# Revit family: Furniture_Table_Spacestor_Arc Boardroom Table
name_source: partatom
category: Furniture
revit_build: Autodesk Revit 2015 (Build: 20140223_1515(x64)
units: mm (PartAtom-declared; Revit-internal decimal feet)

## types (23) — shared parameters
Polished Steel = Spacestor Polished Steel
Table Top = Spacestor White

## per-type parameters (varying)
| type | A | Boat | Bowed Triangle 1200 | Bowed Triangle 800 | Double D End | Leg Length | Leg Width | Length | Offset | Oval | P Length | Rectangular | Single Leg | Split Leg | Split Leg Length | Width |
| rectangular - 1800w x 800d x 720h | 750 mm  [stored 2.46063 ft] | No | No | No | No | 1700 mm  [stored 5.57743 ft] | 700 mm  [stored 2.29659 ft] | 1800 mm  [stored 5.90551 ft] | 520 mm | No | 770 mm  [stored 2.52625 ft] | Yes | Yes | No | 1700 mm  [stored 5.57743 ft] | 800 mm  [stored 2.62467 ft] |
| rectangular - 2000w x 1000d x 720h | 750 mm  [stored 2.46063 ft] | No | No | No | No | 1900 mm  [stored 6.2336 ft] | 900 mm  [stored 2.95276 ft] | 2000 mm  [stored 6.56168 ft] | 520 mm | No | 770 mm  [stored 2.52625 ft] | Yes | Yes | No | 1900 mm  [stored 6.2336 ft] | 1000 mm  [stored 3.28084 ft] |
| rectangular - 2400w x 1200d x 720h | 750 mm  [stored 2.46063 ft] | No | No | No | No | 2300 mm | 1100 mm | 2400 mm | 50 mm  [stored 0.164042 ft] | No | 770 mm  [stored 2.52625 ft] | Yes | Yes | No | 2300 mm | 1200 mm |
| rectangular - 3000w x 1200d x 720h | 800 mm  [stored 2.62467 ft] | No | No | No | No | 2900 mm  [stored 9.51444 ft] | 1100 mm | 3000 mm  [stored 9.84252 ft] | 20 mm  [stored 0.0656168 ft] | No | 770 mm  [stored 2.52625 ft] | Yes | No | Yes | 1400 mm  [stored 4.59318 ft] | 1200 mm |
| rectangular - 3600w x 1200d x 720h | 1100 mm | No | No | No | No | 3500 mm  [stored 11.4829 ft] | 1100 mm | 3600 mm  [stored 11.811 ft] | 20 mm  [stored 0.0656168 ft] | No | 770 mm  [stored 2.52625 ft] | Yes | No | Yes | 1700 mm  [stored 5.57743 ft] | 1200 mm |
| rectangular - 4800w x 1200d x 720h | 1200 mm | No | No | No | No | 4700 mm | 1100 mm | 4800 mm | 520 mm | No | 770 mm  [stored 2.52625 ft] | Yes | No | Yes | 2300 mm | 1200 mm |
| oval-shaped - 2000w x 1000d x 720h | 750 mm  [stored 2.46063 ft] | No | No | No | No | 1300 mm  [stored 4.26509 ft] | 600 mm  [stored 1.9685 ft] | 2000 mm  [stored 6.56168 ft] | 520 mm | Yes | 770 mm  [stored 2.52625 ft] | No | Yes | No | 1900 mm  [stored 6.2336 ft] | 1000 mm  [stored 3.28084 ft] |
| oval-shaped - 2400w x 1200d x 720h | 750 mm  [stored 2.46063 ft] | No | No | No | No | 1700 mm  [stored 5.57743 ft] | 800 mm  [stored 2.62467 ft] | 2400 mm | 520 mm | Yes | 770 mm  [stored 2.52625 ft] | No | Yes | No | 2300 mm | 1200 mm |
| oval-shaped - 3000w x 1200d x 720h | 750 mm  [stored 2.46063 ft] | No | No | No | No | 2300 mm | 800 mm  [stored 2.62467 ft] | 3000 mm  [stored 9.84252 ft] | 520 mm | Yes | 770 mm  [stored 2.52625 ft] | No | Yes | No | 2900 mm  [stored 9.51444 ft] | 1200 mm |
| oval-shaped - 3600w x 1200d x 720h | 750 mm  [stored 2.46063 ft] | No | No | No | No | 2900 mm  [stored 9.51444 ft] | 800 mm  [stored 2.62467 ft] | 3600 mm  [stored 11.811 ft] | 20 mm  [stored 0.0656168 ft] | Yes | 770 mm  [stored 2.52625 ft] | No | No | Yes | 1100 mm | 1200 mm |
| oval-shaped - 4800w x 1200d x 720h | 750 mm  [stored 2.46063 ft] | No | No | No | No | 4100 mm  [stored 13.4514 ft] | 800 mm  [stored 2.62467 ft] | 4800 mm | 520 mm | Yes | 770 mm  [stored 2.52625 ft] | No | No | Yes | 1700 mm  [stored 5.57743 ft] | 1200 mm |
| double d-ended - 2000w x 1200d x 720h | 750 mm  [stored 2.46063 ft] | No | No | No | Yes | 1400 mm  [stored 4.59318 ft] | 1000 mm  [stored 3.28084 ft] | 2000 mm  [stored 6.56168 ft] | 520 mm | No | 770 mm  [stored 2.52625 ft] | No | Yes | No | 1900 mm  [stored 6.2336 ft] | 1200 mm |
| double d-ended - 2400w x 1200d x 720h | 750 mm  [stored 2.46063 ft] | No | No | No | Yes | 1800 mm  [stored 5.90551 ft] | 1000 mm  [stored 3.28084 ft] | 2400 mm | 520 mm | No | 770 mm  [stored 2.52625 ft] | No | Yes | No | 2300 mm | 1200 mm |
| double d-ended - 3000w x 1200d x 720h | 750 mm  [stored 2.46063 ft] | No | No | No | Yes | 2400 mm | 1000 mm  [stored 3.28084 ft] | 3000 mm  [stored 9.84252 ft] | 520 mm | No | 770 mm  [stored 2.52625 ft] | No | Yes | No | 2900 mm  [stored 9.51444 ft] | 1200 mm |
| double d-ended - 3600w x 1200d x 720h | 900 mm  [stored 2.95276 ft] | No | No | No | Yes | 3000 mm  [stored 9.84252 ft] | 1000 mm  [stored 3.28084 ft] | 3600 mm  [stored 11.811 ft] | 20 mm  [stored 0.0656168 ft] | No | 770 mm  [stored 2.52625 ft] | No | No | Yes | 1450 mm  [stored 4.75722 ft] | 1200 mm |
| double d-ended - 4800w x 1200d x 720h | 750 mm  [stored 2.46063 ft] | No | No | No | Yes | 4200 mm | 1000 mm  [stored 3.28084 ft] | 4800 mm | 520 mm | No | 770 mm  [stored 2.52625 ft] | No | No | Yes | 2050 mm  [stored 6.72572 ft] | 1200 mm |
| boat-shaped - 2000w x 1000_800d x 720h | 750 mm  [stored 2.46063 ft] | Yes | No | No | No | 1900 mm  [stored 6.2336 ft] | 800 mm  [stored 2.62467 ft] | 2000 mm  [stored 6.56168 ft] | 520 mm | No | 770 mm  [stored 2.52625 ft] | No | Yes | No | 1900 mm  [stored 6.2336 ft] | 1000 mm  [stored 3.28084 ft] |
| boat-shaped - 2400w x 1200_1000d x 720h | 750 mm  [stored 2.46063 ft] | Yes | No | No | No | 2300 mm | 1000 mm  [stored 3.28084 ft] | 2400 mm | 520 mm | No | 770 mm  [stored 2.52625 ft] | No | Yes | No | 2300 mm | 1200 mm |
| boat-shaped - 3000w x 1200_1000d x 720h | 850 mm  [stored 2.78871 ft] | Yes | No | No | No | 2900 mm  [stored 9.51444 ft] | 1000 mm  [stored 3.28084 ft] | 3000 mm  [stored 9.84252 ft] | 20 mm  [stored 0.0656168 ft] | No | 770 mm  [stored 2.52625 ft] | No | No | Yes | 1400 mm  [stored 4.59318 ft] | 1200 mm |
| boat-shaped - 3600w x 1200_1000d x 720h | 1100 mm | Yes | No | No | No | 3500 mm  [stored 11.4829 ft] | 1000 mm  [stored 3.28084 ft] | 3600 mm  [stored 11.811 ft] | 20 mm  [stored 0.0656168 ft] | No | 770 mm  [stored 2.52625 ft] | No | No | Yes | 1700 mm  [stored 5.57743 ft] | 1200 mm |
| boat-shaped - 4800w x 1200_1000d x 720h | 1200 mm | Yes | No | No | No | 4700 mm | 1000 mm  [stored 3.28084 ft] | 4800 mm | 520 mm | No | 770 mm  [stored 2.52625 ft] | No | No | Yes | 2300 mm | 1200 mm |
| bowed triangle-shaped - 1200w x 1200d x 720h | 750 mm  [stored 2.46063 ft] | No | Yes | No | No | 4700 mm | 1100 mm | 4800 mm | 520 mm | No | 950 mm  [stored 3.1168 ft] | No | No | No | 4700 mm | 1200 mm |
| bowed triangle-shaped - 800w x 800d x 720h | 750 mm  [stored 2.46063 ft] | No | No | Yes | No | 4700 mm | 1100 mm | 4800 mm | 520 mm | No | 750 mm  [stored 2.46063 ft] | No | No | No | 4700 mm | 1200 mm |

note: [stored X ft] marks values corroborated as IEEE doubles in the binary element streams (Revit-internal decimal feet)

## geometry (parser evidence)
native form markers: Sweep x15
no freeform markers — native parametric forms only
